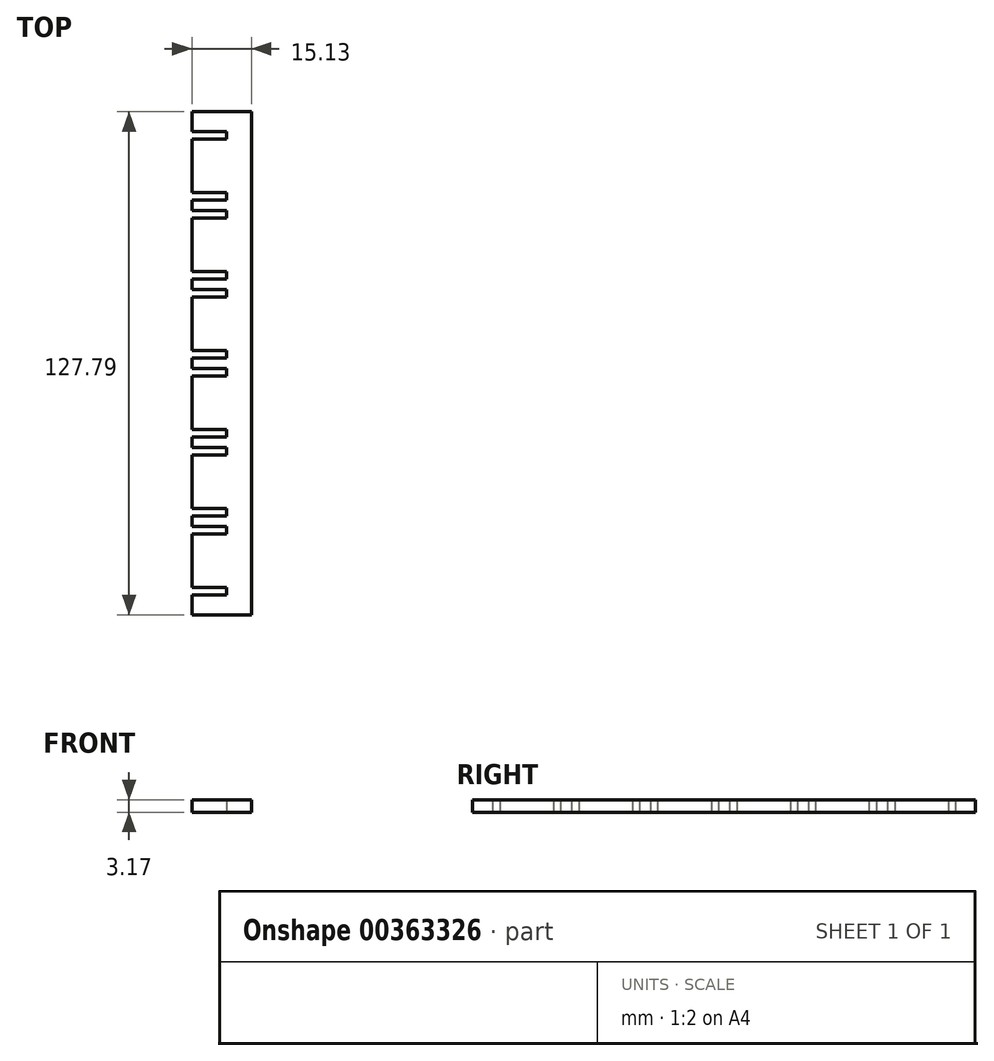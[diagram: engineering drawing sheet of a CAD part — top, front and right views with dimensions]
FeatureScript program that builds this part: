
annotation { "Feature Type Name" : "Feature", "Feature Type Description" : "" }
export const myFeature = defineFeature(function(context is Context, id is Id, definition is map)
    precondition{}
    {
        {
            var Q0;
            Q0=qCreatedBy(makeId("Top.planeOp"),FACE);
            var sketch = newSketch(context, id + "F0", { "sketchPlane" : qUnion([Q0])});
            skPoint(sketch, "E0.middle", {"position": v(0, 0) * mm});
            skLineSegment(sketch, "E1.bottom", {"start": v(2.94, 56.96) * mm, "end": v(-5.84, 56.96) * mm});
            skLineSegment(sketch, "E1.top", {"start": v(2.94, 43.37) * mm, "end": v(-5.84, 43.37) * mm});
            skLineSegment(sketch, "E1.left", {"start": v(2.94, 56.96) * mm, "end": v(2.94, 43.37) * mm});
            skLineSegment(sketch, "E1.right", {"start": v(-5.84, 56.96) * mm, "end": v(-5.84, 43.37) * mm});
            skLineSegment(sketch, "E2.bottom", {"start": v(2.94, 41.51) * mm, "end": v(-5.84, 41.51) * mm});
            skLineSegment(sketch, "E2.top", {"start": v(2.94, 38.74) * mm, "end": v(-5.84, 38.74) * mm});
            skLineSegment(sketch, "E2.left", {"start": v(2.94, 41.51) * mm, "end": v(2.94, 38.74) * mm});
            skLineSegment(sketch, "E2.right", {"start": v(-5.84, 41.51) * mm, "end": v(-5.84, 38.74) * mm});
            skLineSegment(sketch, "E3.bottom", {"start": v(2.94, 36.89) * mm, "end": v(-5.84, 36.89) * mm});
            skLineSegment(sketch, "E3.top", {"start": v(2.94, 23.3) * mm, "end": v(-5.84, 23.3) * mm});
            skLineSegment(sketch, "E3.left", {"start": v(2.94, 36.89) * mm, "end": v(2.94, 23.3) * mm});
            skLineSegment(sketch, "E3.right", {"start": v(-5.84, 36.89) * mm, "end": v(-5.84, 23.3) * mm});
            skLineSegment(sketch, "E4.bottom", {"start": v(2.94, 21.45) * mm, "end": v(-5.84, 21.45) * mm});
            skLineSegment(sketch, "E4.top", {"start": v(2.94, 18.68) * mm, "end": v(-5.84, 18.68) * mm});
            skLineSegment(sketch, "E4.left", {"start": v(2.94, 21.45) * mm, "end": v(2.94, 18.68) * mm});
            skLineSegment(sketch, "E4.right", {"start": v(-5.84, 21.45) * mm, "end": v(-5.84, 18.68) * mm});
            skLineSegment(sketch, "E5.bottom", {"start": v(2.94, 16.82) * mm, "end": v(-5.84, 16.82) * mm});
            skLineSegment(sketch, "E5.top", {"start": v(2.94, 3.23) * mm, "end": v(-5.84, 3.23) * mm});
            skLineSegment(sketch, "E5.left", {"start": v(2.94, 16.82) * mm, "end": v(2.94, 3.23) * mm});
            skLineSegment(sketch, "E5.right", {"start": v(-5.84, 16.82) * mm, "end": v(-5.84, 3.23) * mm});
            skLineSegment(sketch, "E6.bottom", {"start": v(2.94, 1.38) * mm, "end": v(-5.84, 1.38) * mm});
            skLineSegment(sketch, "E6.top", {"start": v(2.94, -1.39) * mm, "end": v(-5.84, -1.39) * mm});
            skLineSegment(sketch, "E6.left", {"start": v(2.94, 1.38) * mm, "end": v(2.94, -1.39) * mm});
            skLineSegment(sketch, "E6.right", {"start": v(-5.84, 1.38) * mm, "end": v(-5.84, -1.39) * mm});
            skLineSegment(sketch, "E7.bottom", {"start": v(2.94, -3.24) * mm, "end": v(-5.84, -3.24) * mm});
            skLineSegment(sketch, "E7.top", {"start": v(2.94, -16.83) * mm, "end": v(-5.84, -16.83) * mm});
            skLineSegment(sketch, "E7.left", {"start": v(2.94, -3.24) * mm, "end": v(2.94, -16.83) * mm});
            skLineSegment(sketch, "E7.right", {"start": v(-5.84, -3.24) * mm, "end": v(-5.84, -16.83) * mm});
            skLineSegment(sketch, "E8.bottom", {"start": v(2.94, -18.69) * mm, "end": v(-5.84, -18.69) * mm});
            skLineSegment(sketch, "E8.top", {"start": v(2.94, -21.45) * mm, "end": v(-5.84, -21.45) * mm});
            skLineSegment(sketch, "E8.left", {"start": v(2.94, -18.69) * mm, "end": v(2.94, -21.45) * mm});
            skLineSegment(sketch, "E8.right", {"start": v(-5.84, -18.69) * mm, "end": v(-5.84, -21.45) * mm});
            skLineSegment(sketch, "E9.bottom", {"start": v(2.94, -23.3) * mm, "end": v(-5.84, -23.3) * mm});
            skLineSegment(sketch, "E9.top", {"start": v(2.94, -36.9) * mm, "end": v(-5.84, -36.9) * mm});
            skLineSegment(sketch, "E9.left", {"start": v(2.94, -23.3) * mm, "end": v(2.94, -36.9) * mm});
            skLineSegment(sketch, "E9.right", {"start": v(-5.84, -23.3) * mm, "end": v(-5.84, -36.9) * mm});
            skLineSegment(sketch, "E10.bottom", {"start": v(2.94, -38.75) * mm, "end": v(-5.84, -38.75) * mm});
            skLineSegment(sketch, "E10.top", {"start": v(2.94, -41.52) * mm, "end": v(-5.84, -41.52) * mm});
            skLineSegment(sketch, "E10.left", {"start": v(2.94, -38.75) * mm, "end": v(2.94, -41.52) * mm});
            skLineSegment(sketch, "E10.right", {"start": v(-5.84, -38.75) * mm, "end": v(-5.84, -41.52) * mm});
            skLineSegment(sketch, "E11.bottom", {"start": v(2.94, -43.37) * mm, "end": v(-5.84, -43.37) * mm});
            skLineSegment(sketch, "E11.top", {"start": v(2.94, -56.96) * mm, "end": v(-5.84, -56.96) * mm});
            skLineSegment(sketch, "E11.left", {"start": v(2.94, -43.37) * mm, "end": v(2.94, -56.96) * mm});
            skLineSegment(sketch, "E11.right", {"start": v(-5.84, -43.37) * mm, "end": v(-5.84, -56.96) * mm});
            skLineSegment(sketch, "E12.left", {"start": v(2.94, -58.82) * mm, "end": v(2.94, -63.9) * mm});
            skLineSegment(sketch, "E12.right", {"start": v(-5.84, -58.82) * mm, "end": v(-5.84, -63.9) * mm});
            skLineSegment(sketch, "E13.bottom", {"start": v(2.94, 58.8) * mm, "end": v(-5.84, 58.8) * mm});
            skLineSegment(sketch, "E13.top", {"start": v(2.94, 63.89) * mm, "end": v(-5.84, 63.89) * mm});
            skLineSegment(sketch, "E13.left", {"start": v(2.94, 58.8) * mm, "end": v(2.94, 63.89) * mm});
            skLineSegment(sketch, "E13.right", {"start": v(-5.84, 58.8) * mm, "end": v(-5.84, 63.89) * mm});
            skLineSegment(sketch, "E14.bottom", {"start": v(2.94, -58.82) * mm, "end": v(-5.84, -58.82) * mm});
            skLineSegment(sketch, "E14.top", {"start": v(2.94, -63.9) * mm, "end": v(-5.84, -63.9) * mm});
            skLineSegment(sketch, "E15.bottom", {"start": v(2.94, -63.9) * mm, "end": v(9.3, -63.9) * mm});
            skLineSegment(sketch, "E15.top", {"start": v(2.94, 63.89) * mm, "end": v(9.3, 63.89) * mm});
            skLineSegment(sketch, "E15.left", {"start": v(2.94, -63.9) * mm, "end": v(2.94, 63.89) * mm});
            skLineSegment(sketch, "E15.right", {"start": v(9.3, -63.9) * mm, "end": v(9.3, 63.89) * mm});
            skSolve(sketch);
        }
        {
            var Q0;
            {var subQ0=sQuery(id+"F0.wireOp",EDGE,"E13.bottom");Q0=makeQuery(id+"F0.imprint","IMPRINT",FACE,{"disambiguationData":[TD([[makeQuery(id+"F0.imprint","IMPRINT",EDGE,{"derivedFrom":subQ0}),-1.0]])]});}
            var Q1;
            {var subQ16=sQuery(id+"F0.wireOp",EDGE,"E15.bottom");Q1=makeQuery(id+"F0.imprint","IMPRINT",FACE,{"disambiguationData":[TD([[makeQuery(id+"F0.imprint","IMPRINT",EDGE,{"derivedFrom":subQ16}),1.0]])]});}
            var Q2;
            {var subQ0=sQuery(id+"F0.wireOp",EDGE,"E1.bottom");Q2=makeQuery(id+"F0.imprint","IMPRINT",FACE,{"disambiguationData":[TD([[makeQuery(id+"F0.imprint","IMPRINT",EDGE,{"derivedFrom":subQ0}),1.0]])]});}
            var Q3;
            {var subQ0=sQuery(id+"F0.wireOp",EDGE,"E2.bottom");Q3=makeQuery(id+"F0.imprint","IMPRINT",FACE,{"disambiguationData":[TD([[makeQuery(id+"F0.imprint","IMPRINT",EDGE,{"derivedFrom":subQ0}),1.0]])]});}
            var Q4;
            {var subQ0=sQuery(id+"F0.wireOp",EDGE,"E3.bottom");Q4=makeQuery(id+"F0.imprint","IMPRINT",FACE,{"disambiguationData":[TD([[makeQuery(id+"F0.imprint","IMPRINT",EDGE,{"derivedFrom":subQ0}),1.0]])]});}
            var Q5;
            {var subQ0=sQuery(id+"F0.wireOp",EDGE,"E4.bottom");Q5=makeQuery(id+"F0.imprint","IMPRINT",FACE,{"disambiguationData":[TD([[makeQuery(id+"F0.imprint","IMPRINT",EDGE,{"derivedFrom":subQ0}),1.0]])]});}
            var Q6;
            {var subQ0=sQuery(id+"F0.wireOp",EDGE,"E5.bottom");Q6=makeQuery(id+"F0.imprint","IMPRINT",FACE,{"disambiguationData":[TD([[makeQuery(id+"F0.imprint","IMPRINT",EDGE,{"derivedFrom":subQ0}),1.0]])]});}
            var Q7;
            {var subQ0=sQuery(id+"F0.wireOp",EDGE,"E6.bottom");Q7=makeQuery(id+"F0.imprint","IMPRINT",FACE,{"disambiguationData":[TD([[makeQuery(id+"F0.imprint","IMPRINT",EDGE,{"derivedFrom":subQ0}),1.0]])]});}
            var Q8;
            {var subQ0=sQuery(id+"F0.wireOp",EDGE,"E7.bottom");Q8=makeQuery(id+"F0.imprint","IMPRINT",FACE,{"disambiguationData":[TD([[makeQuery(id+"F0.imprint","IMPRINT",EDGE,{"derivedFrom":subQ0}),1.0]])]});}
            var Q9;
            {var subQ0=sQuery(id+"F0.wireOp",EDGE,"E8.bottom");Q9=makeQuery(id+"F0.imprint","IMPRINT",FACE,{"disambiguationData":[TD([[makeQuery(id+"F0.imprint","IMPRINT",EDGE,{"derivedFrom":subQ0}),1.0]])]});}
            var Q10;
            {var subQ0=sQuery(id+"F0.wireOp",EDGE,"E9.bottom");Q10=makeQuery(id+"F0.imprint","IMPRINT",FACE,{"disambiguationData":[TD([[makeQuery(id+"F0.imprint","IMPRINT",EDGE,{"derivedFrom":subQ0}),1.0]])]});}
            var Q11;
            {var subQ0=sQuery(id+"F0.wireOp",EDGE,"E10.bottom");Q11=makeQuery(id+"F0.imprint","IMPRINT",FACE,{"disambiguationData":[TD([[makeQuery(id+"F0.imprint","IMPRINT",EDGE,{"derivedFrom":subQ0}),1.0]])]});}
            var Q12;
            {var subQ0=sQuery(id+"F0.wireOp",EDGE,"E11.bottom");Q12=makeQuery(id+"F0.imprint","IMPRINT",FACE,{"disambiguationData":[TD([[makeQuery(id+"F0.imprint","IMPRINT",EDGE,{"derivedFrom":subQ0}),1.0]])]});}
            var Q13;
            Q13=makeQuery(id+"F0.imprint","IMPRINT",FACE,{"disambiguationData":[TD([[makeQuery(id+"F0.imprint","IMPRINT",EDGE,{"derivedFrom":sQuery(id+"F0.wireOp",EDGE,"E12.right")}),1.0]])]});
            extrude(context, id + "F1", {"entities" : qUnion([Q0, Q1, Q2, Q3, Q4, Q5, Q6, Q7, Q8, Q9, Q10, Q11, Q12, Q13]), "depth" : 3.17 * mm});
        }
    });
